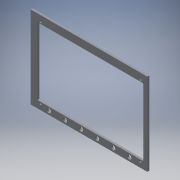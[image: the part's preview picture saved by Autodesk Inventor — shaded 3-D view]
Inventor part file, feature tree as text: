
AUTODESK INVENTOR PART (.ipt)
format: ipt  version: 2019 (Build 230136000, 136)  size: 140,800 bytes
history: native  units: in
note: dims shown in document units (in); Inventor stores cm internally (conversion verified against a paired STEP export)
features: reference x18, plane x2, other x2, sketch x1, extrude x1
ambient origin geometry x8: Origin, YZ Plane, XZ Plane, XY Plane, X Axis, Y Axis, Z Axis, Center Point
bodies: Body1 (feature_tree)
feature tree (24):
  plane  "Work Plane1"
  sketch  "Sketch1"  dims[d1=5.125in d2=7.25in d3=0.5in d4=0.2677in d5=2.3622in d7=1.0in d8=0.3937in d10=1.0in d18=0.05in d19=0.125in d20=0.0in]
  plane  "Work Plane2"
  extrude  "Extrusion2"  Depth=7.25in
  reference  "Reference1"
  reference  "Reference2"
  reference  "Reference3"
  reference  "Reference4"
  reference  "Reference5"
  reference  "Reference6"
  reference  "Reference7"
  reference  "Reference8"
  reference  "Reference9"
  reference  "Reference10"
  reference  "Reference11"
  reference  "Reference12"
  reference  "Reference13"
  reference  "Reference14"
  reference  "Reference15"
  reference  "Reference16"
  reference  "Reference17"
  reference  "Reference18"
  other  "Assembly1"
  other  "NHD-7:1"
